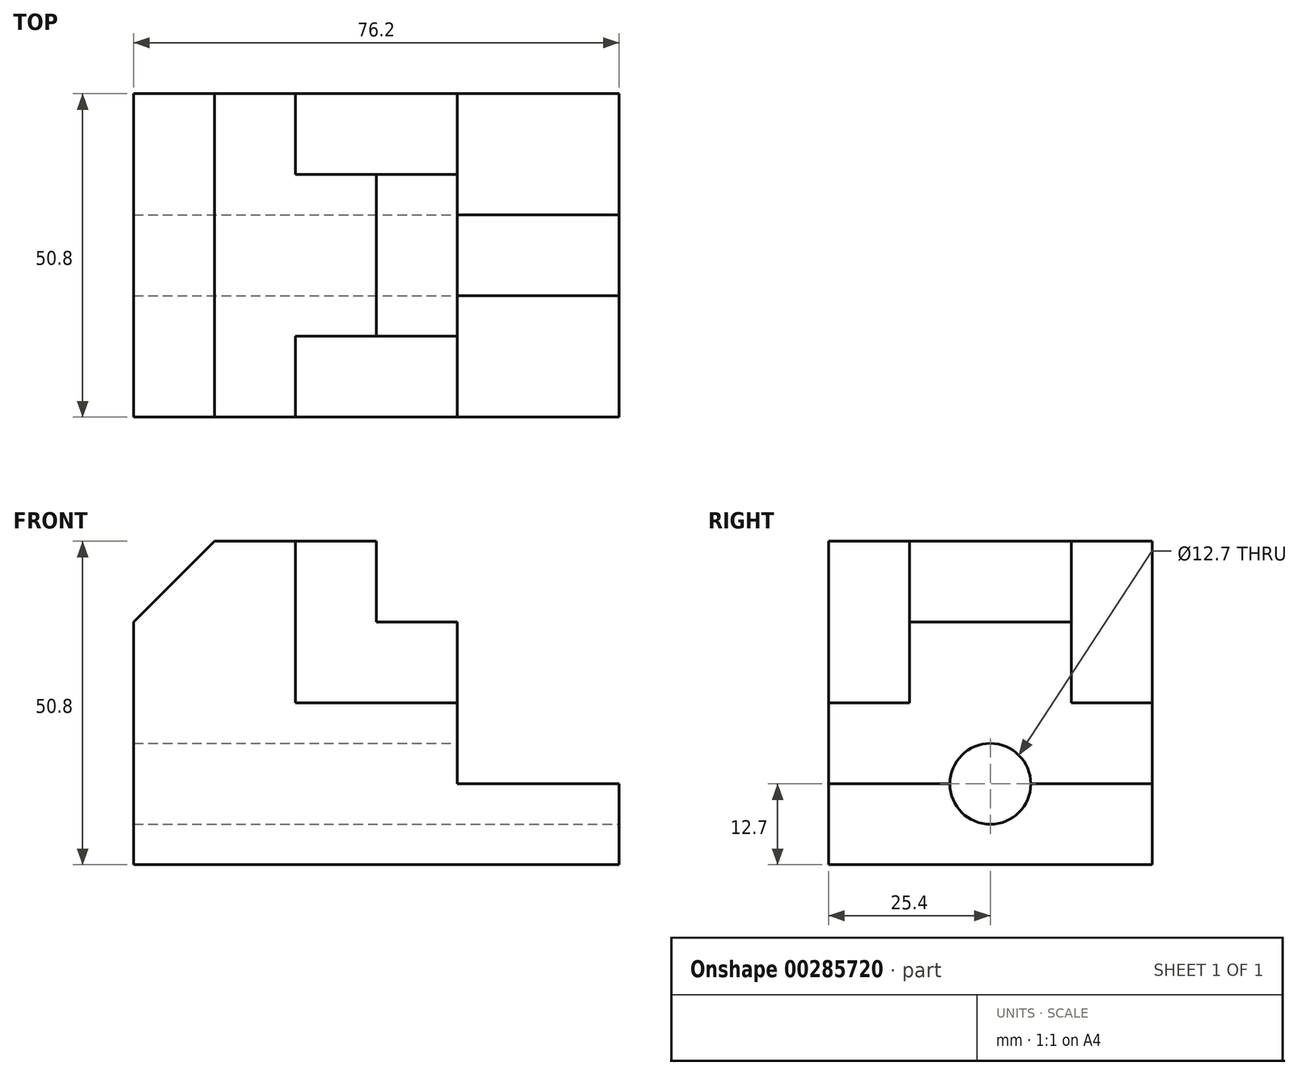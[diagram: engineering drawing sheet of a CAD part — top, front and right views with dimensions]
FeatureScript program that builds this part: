
annotation { "Feature Type Name" : "Feature", "Feature Type Description" : "" }
export const myFeature = defineFeature(function(context is Context, id is Id, definition is map)
    precondition{}
    {
        {
            var Q0;
            Q0=qCreatedBy(makeId("Front.planeOp"),FACE);
            var sketch = newSketch(context, id + "F0", { "sketchPlane" : qUnion([Q0])});
            skLineSegment(sketch, "E0", {"start": v(0, 0) * mm, "end": v(-76.2, 0) * mm});
            skLineSegment(sketch, "E1", {"start": v(0, 0) * mm, "end": v(0, 12.7) * mm});
            skLineSegment(sketch, "E2", {"start": v(0, 12.7) * mm, "end": v(-25.4, 12.7) * mm});
            skLineSegment(sketch, "E3", {"start": v(-50.8, 50.8) * mm, "end": v(-63.5, 50.8) * mm});
            skLineSegment(sketch, "E4", {"start": v(-63.5, 50.8) * mm, "end": v(-76.2, 38.1) * mm});
            skLineSegment(sketch, "E5", {"start": v(-76.2, 38.1) * mm, "end": v(-76.2, 0) * mm});
            skLineSegment(sketch, "E6", {"start": v(-25.4, 12.7) * mm, "end": v(-25.4, 25.4) * mm});
            skLineSegment(sketch, "E7", {"start": v(-25.4, 25.4) * mm, "end": v(-50.8, 25.4) * mm});
            skLineSegment(sketch, "E8", {"start": v(-50.8, 25.4) * mm, "end": v(-50.8, 50.8) * mm});
            skPoint(sketch, "E9.orphan", {"position": v(-38.1, 50.8) * mm});
            skSolve(sketch);
        }
        {
            var Q0;
            Q0=makeQuery(id+"F0.imprint","IMPRINT",FACE,{"disambiguationData":[TD([[makeQuery(id+"F0.imprint","IMPRINT",EDGE,{"derivedFrom":sQuery(id+"F0.wireOp",EDGE,"E0")}),-1.0]])]});
            extrude(context, id + "F1", {"entities" : qUnion([Q0]), "depth" : 50.8 * mm});
        }
        {
            var Q0;
            Q0=makeQuery(id+"F1.opExtrude","CAP_FACE",FACE,{"disambiguationData":[OSD([sQuery(id+"F0.wireOp",EDGE,"E0"),sQuery(id+"F0.wireOp",EDGE,"E1"),sQuery(id+"F0.wireOp",EDGE,"E2"),sQuery(id+"F0.wireOp",EDGE,"IaRwlvuf-RyZV-WDcQ-tqNH-Czdv5lfhXuUS"),sQuery(id+"F0.wireOp",EDGE,"AVSXDXer-e9iS-IohA-yLMA-Z6J06gi4UY4s"),sQuery(id+"F0.wireOp",EDGE,"MBXUd53v-bAr5-71Ia-ppZq-Rwgg3m1Y8P94"),sQuery(id+"F0.wireOp",EDGE,"E3"),sQuery(id+"F0.wireOp",EDGE,"E4"),sQuery(id+"F0.wireOp",EDGE,"E5")])],"isStart":false});
            cPlane(context, id + "F2", {"entities" : qUnion([Q0]), "cplaneType" : CPlaneType.OFFSET, "offset" : 12.7 * mm, "oppositeDirection" : true, "width" : 152.4 * mm, "height" : 152.4 * mm});
        }
        {
            var Q0;
            Q0=qCreatedBy(id+"F2.planeOp",FACE);
            var sketch = newSketch(context, id + "F3", { "sketchPlane" : qUnion([Q0])});
            skLineSegment(sketch, "E10", {"start": v(-50.8, 50.8) * mm, "end": v(-38.1, 50.8) * mm});
            skLineSegment(sketch, "E11", {"start": v(-38.1, 50.8) * mm, "end": v(-38.1, 38.1) * mm});
            skLineSegment(sketch, "E12", {"start": v(-38.1, 38.1) * mm, "end": v(-25.4, 38.1) * mm});
            skLineSegment(sketch, "E13", {"start": v(-25.4, 38.1) * mm, "end": v(-25.4, 25.4) * mm});
            skLineSegment(sketch, "E14", {"start": v(-25.4, 25.4) * mm, "end": v(-50.8, 25.4) * mm});
            skLineSegment(sketch, "E15", {"start": v(-50.8, 25.4) * mm, "end": v(-50.8, 50.8) * mm});
            skSolve(sketch);
        }
        {
            var Q0;
            Q0 = qSketchRegion(id + "F3", true);
            extrude(context, id + "F4", {"entities" : qUnion([Q0]), "operationType" : NewBodyOperationType.ADD, "oppositeDirection" : true, "depth" : 25.4 * mm});
        }
        {
            var Q0;
            Q0=makeQuery(id+"F1.opExtrude","SWEPT_FACE",FACE,{"disambiguationData":[OSD([sQuery(id+"F0.wireOp",EDGE,"E1")])]});
            var sketch = newSketch(context, id + "F5", { "sketchPlane" : qUnion([Q0])});
            skCircle(sketch, "E16", {"center": v(-25.4, 12.7) * mm, "radius": 6.35 * mm});
            skSolve(sketch);
        }
        {
            var Q0;
            Q0 = qSketchRegion(id + "F5", true);
            extrude(context, id + "F6", {"entities" : qUnion([Q0]), "operationType" : NewBodyOperationType.REMOVE, "oppositeDirection" : true, "depth" : 76.2 * mm});
        }
    });
